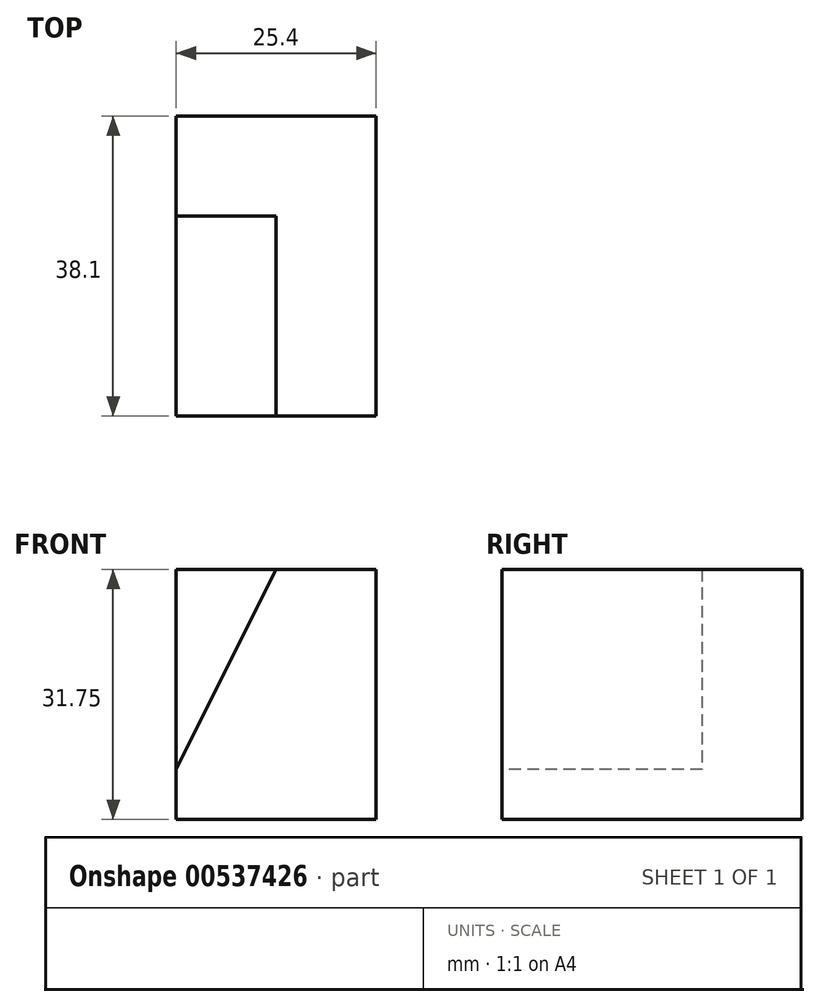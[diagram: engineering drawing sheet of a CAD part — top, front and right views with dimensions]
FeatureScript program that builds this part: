
annotation { "Feature Type Name" : "Feature", "Feature Type Description" : "" }
export const myFeature = defineFeature(function(context is Context, id is Id, definition is map)
    precondition{}
    {
        {
            var Q0;
            Q0=qCreatedBy(makeId("Top.planeOp"),FACE);
            var sketch = newSketch(context, id + "F0", { "sketchPlane" : qUnion([Q0])});
            skLineSegment(sketch, "E0", {"start": v(0, 0) * mm, "end": v(0, 38.1) * mm});
            skLineSegment(sketch, "E1", {"start": v(0, 38.1) * mm, "end": v(25.4, 38.1) * mm});
            skLineSegment(sketch, "E2", {"start": v(25.4, 38.1) * mm, "end": v(25.4, 0) * mm});
            skLineSegment(sketch, "E3", {"start": v(25.4, 0) * mm, "end": v(0, 0) * mm});
            skSolve(sketch);
        }
        {
            var Q0;
            Q0=makeQuery(id+"F0.imprint","IMPRINT",FACE,{"disambiguationData":[TD([[makeQuery(id+"F0.imprint","IMPRINT",EDGE,{"derivedFrom":sQuery(id+"F0.wireOp",EDGE,"E0")}),-1.0]])]});
            extrude(context, id + "F1", {"entities" : qUnion([Q0]), "depth" : 31.75 * mm, "offsetDistance" : 25.4 * mm});
        }
        {
            var Q0;
            Q0=makeQuery(id+"F1.opExtrude","SWEPT_FACE",FACE,{"disambiguationData":[OSD([sQuery(id+"F0.wireOp",EDGE,"E3")])]});
            var sketch = newSketch(context, id + "F2", { "sketchPlane" : qUnion([Q0])});
            skLineSegment(sketch, "E4", {"start": v(12.7, 31.75) * mm, "end": v(0, 31.75) * mm});
            skLineSegment(sketch, "E5", {"start": v(12.7, 31.75) * mm, "end": v(0, 6.35) * mm});
            skLineSegment(sketch, "E6", {"start": v(0, 6.35) * mm, "end": v(0, 31.75) * mm});
            skSolve(sketch);
        }
        {
            var Q0;
            Q0=makeQuery(id+"F2.imprint","IMPRINT",FACE,{"disambiguationData":[TD([[makeQuery(id+"F2.imprint","IMPRINT",EDGE,{"derivedFrom":sQuery(id+"F2.wireOp",EDGE,"E4")}),1.0]])]});
            extrude(context, id + "F3", {"entities" : qUnion([Q0]), "operationType" : NewBodyOperationType.REMOVE, "oppositeDirection" : true, "depth" : 25.4 * mm, "offsetDistance" : 25.4 * mm});
        }
    });
